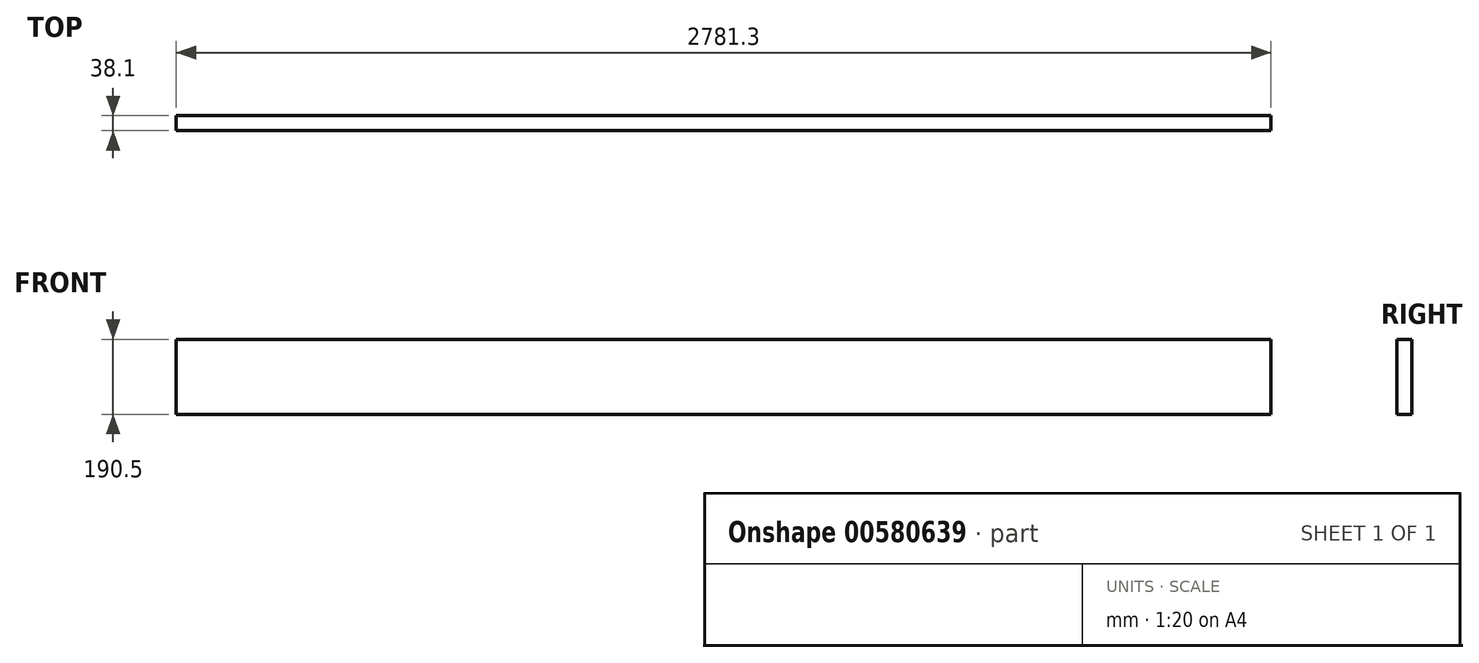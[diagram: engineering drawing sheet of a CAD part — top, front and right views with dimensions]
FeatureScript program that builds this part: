
annotation { "Feature Type Name" : "Feature", "Feature Type Description" : "" }
export const myFeature = defineFeature(function(context is Context, id is Id, definition is map)
    precondition{}
    {
        {
            var Q0;
            Q0=qCreatedBy(makeId("Top.planeOp"),FACE);
            var sketch = newSketch(context, id + "F0", { "sketchPlane" : qUnion([Q0])});
            skLineSegment(sketch, "E0.bottom", {"start": v(-1390.65, -19.05) * mm, "end": v(1390.65, -19.05) * mm});
            skLineSegment(sketch, "E0.top", {"start": v(-1390.65, 19.05) * mm, "end": v(1390.65, 19.05) * mm});
            skLineSegment(sketch, "E0.left", {"start": v(-1390.65, -19.05) * mm, "end": v(-1390.65, 19.05) * mm});
            skLineSegment(sketch, "E0.right", {"start": v(1390.65, -19.05) * mm, "end": v(1390.65, 19.05) * mm});
            skPoint(sketch, "E0.middle", {"position": v(0, 0) * mm});
            skSolve(sketch);
        }
        {
            var Q0;
            Q0=makeQuery(id+"F0.imprint","IMPRINT",FACE,{"disambiguationData":[TD([[makeQuery(id+"F0.imprint","IMPRINT",EDGE,{"derivedFrom":sQuery(id+"F0.wireOp",EDGE,"E0.bottom")}),1.0]])]});
            extrude(context, id + "F1", {"entities" : qUnion([Q0]), "depth" : 190.5 * mm, "offsetDistance" : 25.4 * mm});
        }
    });
